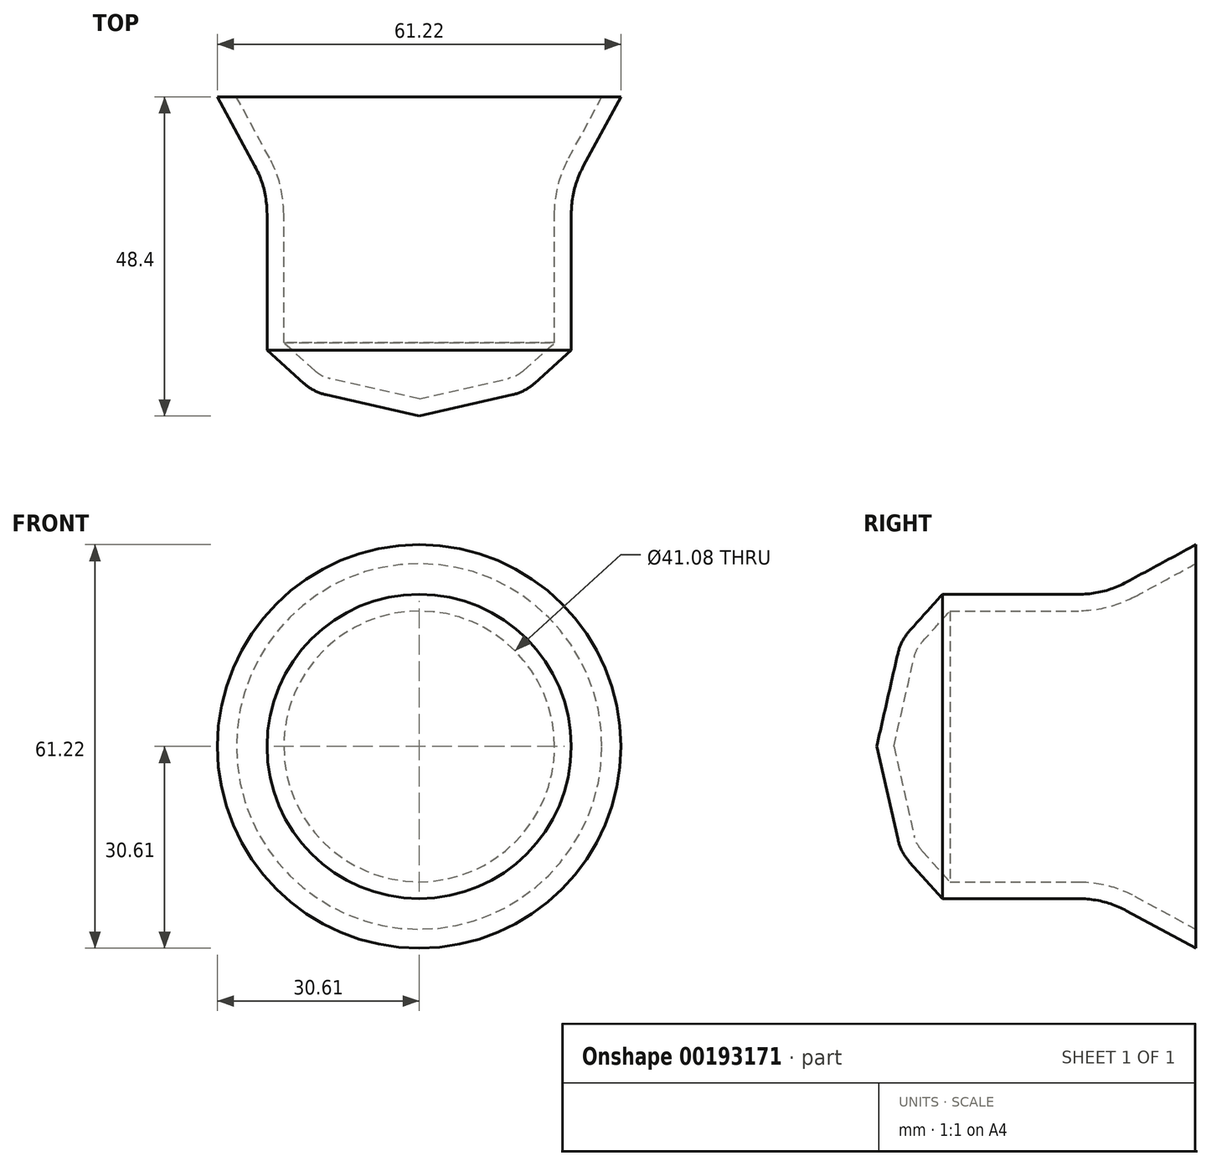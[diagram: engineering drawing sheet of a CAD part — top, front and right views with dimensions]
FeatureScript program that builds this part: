
annotation { "Feature Type Name" : "Feature", "Feature Type Description" : "" }
export const myFeature = defineFeature(function(context is Context, id is Id, definition is map)
    precondition{}
    {
        {
            var Q0;
            Q0=qCreatedBy(makeId("Top.planeOp"),FACE);
            var sketch = newSketch(context, id + "F0", { "sketchPlane" : qUnion([Q0])});
            skLineSegment(sketch, "E0", {"start": v(0, 48.4) * mm, "end": v(30.6, 48.4) * mm});
            skLineSegment(sketch, "E1", {"start": v(30.6, 48.4) * mm, "end": v(24.92, 37.9) * mm});
            skLineSegment(sketch, "E2", {"start": v(23.08, 30.64) * mm, "end": v(23.08, 9.98) * mm});
            skLineSegment(sketch, "E3", {"start": v(23.08, 9.98) * mm, "end": v(17.54, 5) * mm});
            skLineSegment(sketch, "E4", {"start": v(14.14, 3.23) * mm, "end": v(0, 0) * mm});
            skPoint(sketch, "E5.visualSharp", {"position": v(23.08, 34.5) * mm});
            skArc(sketch, "E5.filletArc", {"start": v(24.92, 37.9) * mm, "mid": v(23.55, 34.38) * mm, "end": v(23.08, 30.64) * mm});
            skPoint(sketch, "E6.visualSharp", {"position": v(16.07, 3.67) * mm});
            skArc(sketch, "E6.filletArc", {"start": v(14.14, 3.23) * mm, "mid": v(15.95, 3.9) * mm, "end": v(17.54, 5) * mm});
            skLineSegment(sketch, "E7", {"start": v(0, 48.4) * mm, "end": v(0, 0) * mm});
            skSolve(sketch);
        }
        {
            var Q0;
            Q0=qCreatedBy(makeId("Top.planeOp"),FACE);
            var sketch = newSketch(context, id + "F1", { "sketchPlane" : qUnion([Q0])});
            skSolve(sketch);
        }
        {
            var Q0;
            Q0 = qSketchRegion(id + "F1", true);
            var Q1;
            Q1=makeQuery(id+"F0.imprint","IMPRINT",FACE,{"disambiguationData":[TD([[makeQuery(id+"F0.imprint","IMPRINT",EDGE,{"derivedFrom":sQuery(id+"F0.wireOp",EDGE,"E0")}),-1.0]])]});
            var Q2;
            Q2=sQuery(id+"F0.wireOp",EDGE,"E7");
            revolve(context, id + "F2", {"entities" : qUnion([Q0, Q1]), "axis" : qUnion([Q2]), "revolveType" : RevolveType.FULL});
        }
        {
            var Q0;
            Q0=makeQuery(id+"F2.opRevolve","SWEPT_FACE",FACE,{"disambiguationData":[OSD([sQuery(id+"F0.wireOp",EDGE,"E0")])]});
            shell(context, id + "F3", {"entities" : qUnion([Q0]), "thickness" : 2.54 * mm});
        }
    });
